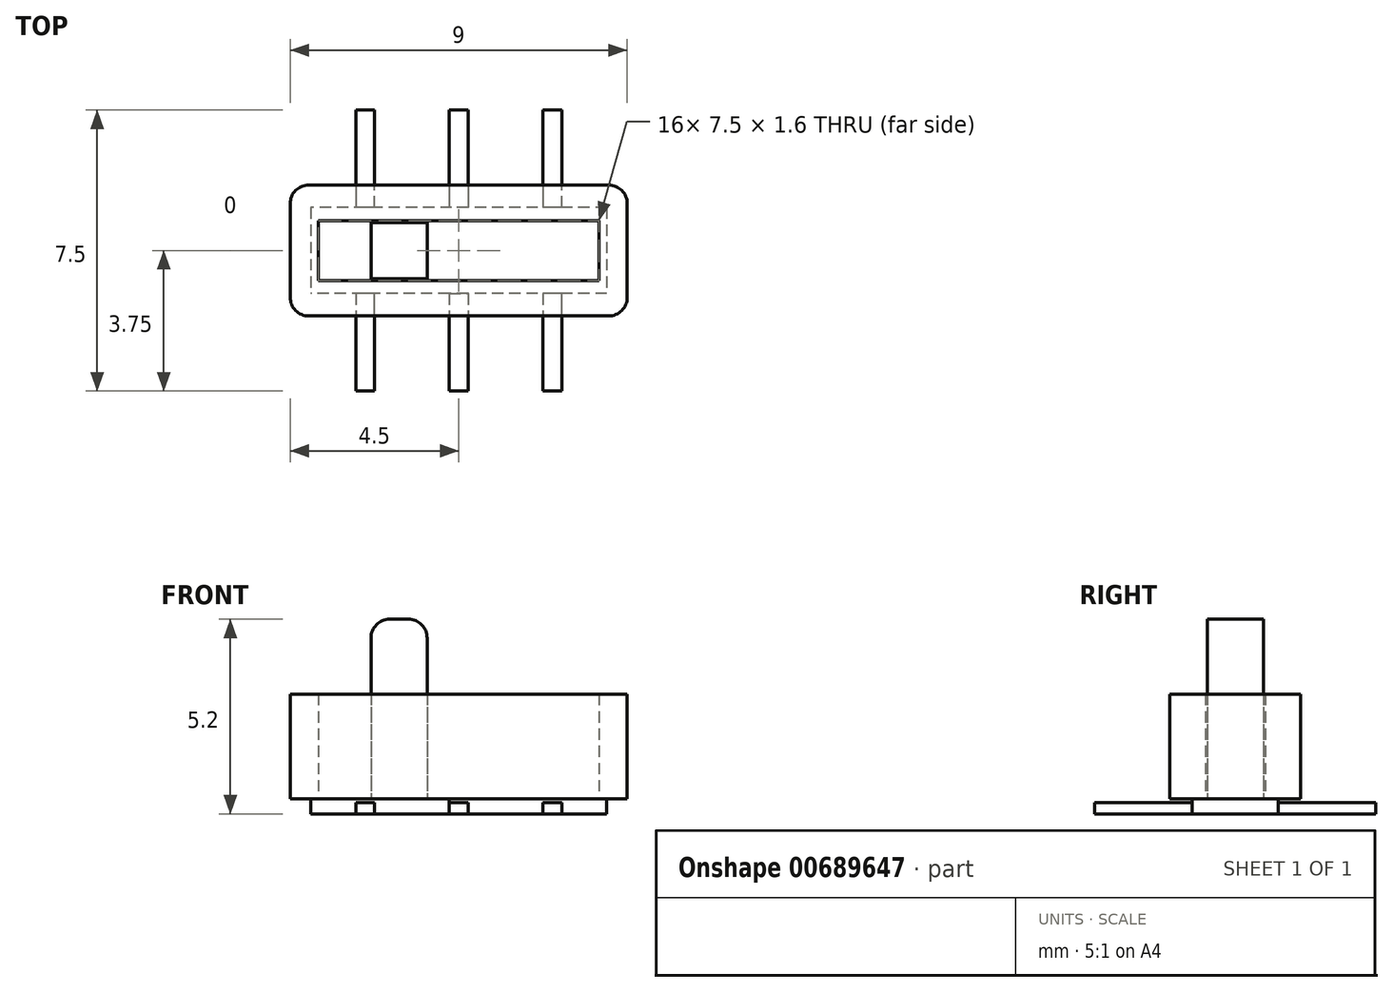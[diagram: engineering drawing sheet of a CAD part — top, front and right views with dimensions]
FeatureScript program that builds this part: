
annotation { "Feature Type Name" : "Feature", "Feature Type Description" : "" }
export const myFeature = defineFeature(function(context is Context, id is Id, definition is map)
    precondition{}
    {
        {
            var Q0;
            Q0=qCreatedBy(makeId("Top.planeOp"),FACE);
            var sketch = newSketch(context, id + "F0", { "sketchPlane" : qUnion([Q0])});
            skLineSegment(sketch, "E0.bottom", {"start": v(3.95, 1.15) * mm, "end": v(-3.95, 1.15) * mm});
            skLineSegment(sketch, "E0.top", {"start": v(3.95, -1.15) * mm, "end": v(-3.95, -1.15) * mm});
            skLineSegment(sketch, "E0.left", {"start": v(3.95, 1.15) * mm, "end": v(3.95, -1.15) * mm});
            skLineSegment(sketch, "E0.right", {"start": v(-3.95, 1.15) * mm, "end": v(-3.95, -1.15) * mm});
            skPoint(sketch, "E0.middle", {"position": v(0, 0) * mm});
            skLineSegment(sketch, "E1", {"start": v(-0.25, 3.75) * mm, "end": v(-0.25, 1.15) * mm});
            skLineSegment(sketch, "E2", {"start": v(0.25, 3.75) * mm, "end": v(0.25, 1.15) * mm});
            skLineSegment(sketch, "E3", {"start": v(-0.25, 3.75) * mm, "end": v(0.25, 3.75) * mm});
            skLineSegment(sketch, "E4", {"start": v(-0.25, -3.75) * mm, "end": v(0.25, -3.75) * mm});
            skLineSegment(sketch, "E5", {"start": v(-0.25, 1.15) * mm, "end": v(0.25, 1.15) * mm});
            skLineSegment(sketch, "E6", {"start": v(-0.25, -1.15) * mm, "end": v(0.25, -1.15) * mm});
            skLineSegment(sketch, "E7.trimOffspring", {"start": v(0.25, -1.15) * mm, "end": v(0.25, -3.75) * mm});
            skLineSegment(sketch, "E8.trimOffspring", {"start": v(-0.25, -1.15) * mm, "end": v(-0.25, -3.75) * mm});
            skLineSegment(sketch, "E9", {"start": v(2.25, 3.75) * mm, "end": v(2.25, 1.15) * mm});
            skLineSegment(sketch, "E10", {"start": v(2.25, -3.75) * mm, "end": v(2.75, -3.75) * mm});
            skLineSegment(sketch, "E11", {"start": v(2.75, -3.75) * mm, "end": v(2.75, -1.15) * mm});
            skLineSegment(sketch, "E12", {"start": v(2.75, 3.75) * mm, "end": v(2.25, 3.75) * mm});
            skLineSegment(sketch, "E13.trimOffspring", {"start": v(2.25, -1.15) * mm, "end": v(2.25, -3.75) * mm});
            skLineSegment(sketch, "E14.trimOffspring", {"start": v(2.75, 1.15) * mm, "end": v(2.75, 3.75) * mm});
            skLineSegment(sketch, "E15", {"start": v(-2.25, -3.75) * mm, "end": v(-2.25, -1.15) * mm});
            skLineSegment(sketch, "E16", {"start": v(-2.25, 3.75) * mm, "end": v(-2.75, 3.75) * mm});
            skLineSegment(sketch, "E17", {"start": v(-2.75, 3.75) * mm, "end": v(-2.75, 1.15) * mm});
            skLineSegment(sketch, "E18", {"start": v(-2.75, -3.75) * mm, "end": v(-2.25, -3.75) * mm});
            skLineSegment(sketch, "E19.trimOffspring", {"start": v(-2.25, 1.15) * mm, "end": v(-2.25, 3.75) * mm});
            skLineSegment(sketch, "E20.trimOffspring", {"start": v(-2.75, -1.15) * mm, "end": v(-2.75, -3.75) * mm});
            skSolve(sketch);
        }
        {
            var Q0;
            Q0=qCreatedBy(makeId("Top.planeOp"),FACE);
            cPlane(context, id + "F1", {"entities" : qUnion([Q0]), "cplaneType" : CPlaneType.OFFSET, "offset" : 0.4 * mm, "width" : 150 * mm, "height" : 150 * mm});
        }
        {
            var Q0;
            Q0=qCreatedBy(id+"F1.planeOp",FACE);
            var sketch = newSketch(context, id + "F2", { "sketchPlane" : qUnion([Q0])});
            skLineSegment(sketch, "E21.bottom", {"start": v(4.5, 1.75) * mm, "end": v(-4.5, 1.75) * mm});
            skLineSegment(sketch, "E21.top", {"start": v(4.5, -1.75) * mm, "end": v(-4.5, -1.75) * mm});
            skLineSegment(sketch, "E21.left", {"start": v(4.5, 1.75) * mm, "end": v(4.5, -1.75) * mm});
            skLineSegment(sketch, "E21.right", {"start": v(-4.5, 1.75) * mm, "end": v(-4.5, -1.75) * mm});
            skPoint(sketch, "E21.middle", {"position": v(0, 0) * mm});
            skLineSegment(sketch, "E22.bottom", {"start": v(-3.75, 0.8) * mm, "end": v(3.75, 0.8) * mm});
            skLineSegment(sketch, "E22.top", {"start": v(-3.75, -0.8) * mm, "end": v(3.75, -0.8) * mm});
            skLineSegment(sketch, "E22.left", {"start": v(-3.75, 0.8) * mm, "end": v(-3.75, -0.8) * mm});
            skLineSegment(sketch, "E22.right", {"start": v(3.75, 0.8) * mm, "end": v(3.75, -0.8) * mm});
            skLineSegment(sketch, "E23.bottom", {"start": v(-0.84, 0.75) * mm, "end": v(-2.34, 0.75) * mm});
            skLineSegment(sketch, "E23.top", {"start": v(-0.84, -0.75) * mm, "end": v(-2.34, -0.75) * mm});
            skLineSegment(sketch, "E23.left", {"start": v(-0.84, 0.75) * mm, "end": v(-0.84, -0.75) * mm});
            skLineSegment(sketch, "E23.right", {"start": v(-2.34, 0.75) * mm, "end": v(-2.34, -0.75) * mm});
            skPoint(sketch, "E23.middle", {"position": v(-1.6, 0) * mm});
            skSolve(sketch);
        }
        {
            var Q0;
            Q0=makeQuery(id+"F2.imprint","IMPRINT",FACE,{"disambiguationData":[TD([[makeQuery(id+"F2.imprint","IMPRINT",EDGE,{"derivedFrom":sQuery(id+"F2.wireOp",EDGE,"E21.bottom")}),1.0]])]});
            extrude(context, id + "F3", {"entities" : qUnion([Q0]), "depth" : 2.8 * mm, "offsetDistance" : 25 * mm});
        }
        {
            var Q0;
            Q0=makeQuery(id+"F0.imprint","IMPRINT",FACE,{"disambiguationData":[TD([[makeQuery(id+"F0.imprint","IMPRINT",EDGE,{"derivedFrom":sQuery(id+"F0.wireOp",EDGE,"E0.bottom")}),1.0]])]});
            extrude(context, id + "F4", {"entities" : qUnion([Q0]), "depth" : 0.4 * mm, "offsetDistance" : 25 * mm});
        }
        {
            var Q0;
            Q0=makeQuery(id+"F2.imprint","IMPRINT",FACE,{"disambiguationData":[TD([[makeQuery(id+"F2.imprint","IMPRINT",EDGE,{"derivedFrom":sQuery(id+"F2.wireOp",EDGE,"E23.bottom")}),1.0]])]});
            extrude(context, id + "F5", {"entities" : qUnion([Q0]), "depth" : 4.8 * mm, "offsetDistance" : 25 * mm});
        }
        {
            var Q0;
            Q0=makeQuery(id+"F0.imprint","IMPRINT",FACE,{"disambiguationData":[TD([[makeQuery(id+"F0.imprint","IMPRINT",EDGE,{"derivedFrom":sQuery(id+"F0.wireOp",EDGE,"E16")}),1.0]])]});
            var Q1;
            Q1=makeQuery(id+"F0.imprint","IMPRINT",FACE,{"disambiguationData":[TD([[makeQuery(id+"F0.imprint","IMPRINT",EDGE,{"derivedFrom":sQuery(id+"F0.wireOp",EDGE,"E1")}),1.0]])]});
            var Q2;
            {var subQ0=sQuery(id+"F0.wireOp",EDGE,"E9");Q2=makeQuery(id+"F0.imprint","IMPRINT",FACE,{"disambiguationData":[TD([[makeQuery(id+"F0.imprint","IMPRINT",EDGE,{"derivedFrom":subQ0}),1.0]])]});}
            var Q3;
            Q3=makeQuery(id+"F0.imprint","IMPRINT",FACE,{"disambiguationData":[TD([[makeQuery(id+"F0.imprint","IMPRINT",EDGE,{"derivedFrom":sQuery(id+"F0.wireOp",EDGE,"E10")}),1.0]])]});
            var Q4;
            {var subQ4=sQuery(id+"F0.wireOp",EDGE,"E4");Q4=makeQuery(id+"F0.imprint","IMPRINT",FACE,{"disambiguationData":[TD([[makeQuery(id+"F0.imprint","IMPRINT",EDGE,{"derivedFrom":subQ4}),1.0]])]});}
            var Q5;
            {var subQ0=sQuery(id+"F0.wireOp",EDGE,"E15");Q5=makeQuery(id+"F0.imprint","IMPRINT",FACE,{"disambiguationData":[TD([[makeQuery(id+"F0.imprint","IMPRINT",EDGE,{"derivedFrom":subQ0}),1.0]])]});}
            extrude(context, id + "F6", {"entities" : qUnion([Q0, Q1, Q2, Q3, Q4, Q5]), "depth" : 0.3 * mm, "offsetDistance" : 25 * mm});
        }
        {
            var Q0;
            Q0=makeQuery(id+"F5.opExtrude","CAP_EDGE",EDGE,{"disambiguationData":[OSD([sQuery(id+"F2.wireOp",EDGE,"E23.right")])],"isStart":false});
            fillet(context, id + "F7", {"entities" : qUnion([Q0]), "radius" : 0.5 * mm, "tangentPropagation" : true, "allowEdgeOverflow" : false});
        }
        {
            var Q0;
            Q0=makeQuery(id+"F5.opExtrude","CAP_EDGE",EDGE,{"disambiguationData":[OSD([sQuery(id+"F2.wireOp",EDGE,"E23.left")])],"isStart":false});
            fillet(context, id + "F8", {"entities" : qUnion([Q0]), "radius" : 0.5 * mm, "tangentPropagation" : true, "allowEdgeOverflow" : false});
        }
        {
            var Q0;
            Q0=makeQuery(id+"F3.opExtrude","SWEPT_EDGE",EDGE,{"disambiguationData":[OSD([sQuery(id+"F2.wireOp",EDGE,"E21.top"),sQuery(id+"F2.wireOp",EDGE,"E21.right")])]});
            fillet(context, id + "F9", {"entities" : qUnion([Q0]), "radius" : 0.5 * mm, "tangentPropagation" : true, "allowEdgeOverflow" : false});
        }
        {
            var Q0;
            Q0=makeQuery(id+"F3.opExtrude","SWEPT_EDGE",EDGE,{"disambiguationData":[OSD([sQuery(id+"F2.wireOp",EDGE,"E21.bottom"),sQuery(id+"F2.wireOp",EDGE,"E21.right")])]});
            fillet(context, id + "F10", {"entities" : qUnion([Q0]), "radius" : 0.5 * mm, "tangentPropagation" : true, "allowEdgeOverflow" : false});
        }
        {
            var Q0;
            Q0=makeQuery(id+"F3.opExtrude","SWEPT_EDGE",EDGE,{"disambiguationData":[OSD([sQuery(id+"F2.wireOp",EDGE,"E21.top"),sQuery(id+"F2.wireOp",EDGE,"E21.left")])]});
            fillet(context, id + "F11", {"entities" : qUnion([Q0]), "radius" : 0.5 * mm, "tangentPropagation" : true, "allowEdgeOverflow" : false});
        }
        {
            var Q0;
            Q0=makeQuery(id+"F3.opExtrude","SWEPT_EDGE",EDGE,{"disambiguationData":[OSD([sQuery(id+"F2.wireOp",EDGE,"E21.bottom"),sQuery(id+"F2.wireOp",EDGE,"E21.left")])]});
            fillet(context, id + "F12", {"entities" : qUnion([Q0]), "radius" : 0.5 * mm, "tangentPropagation" : true, "allowEdgeOverflow" : false});
        }
    });
